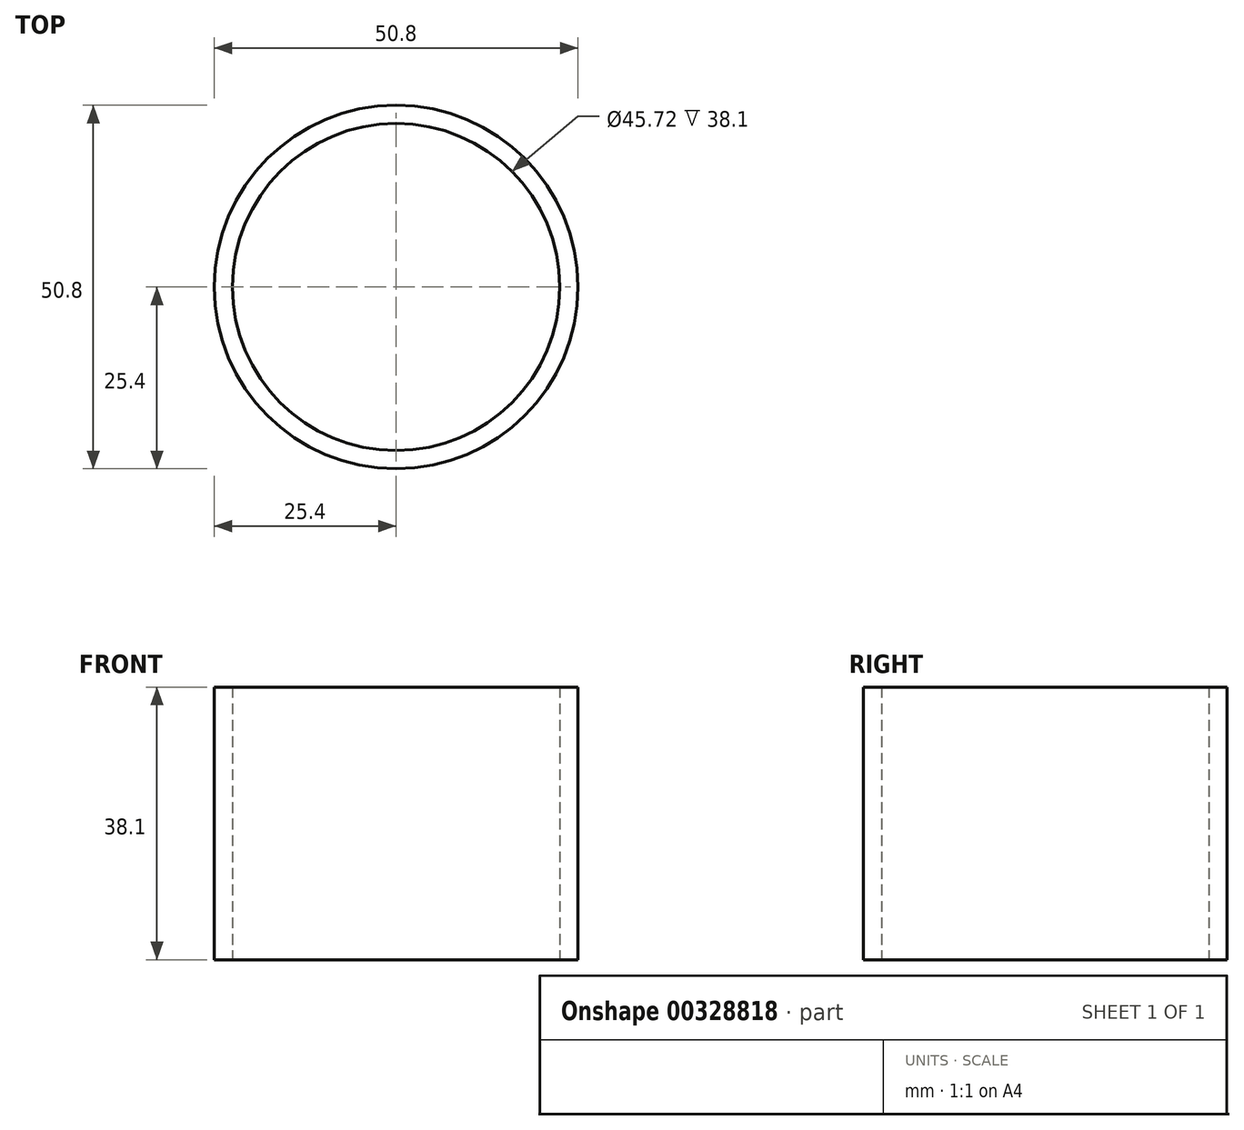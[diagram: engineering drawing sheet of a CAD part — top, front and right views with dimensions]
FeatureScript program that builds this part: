
annotation { "Feature Type Name" : "Feature", "Feature Type Description" : "" }
export const myFeature = defineFeature(function(context is Context, id is Id, definition is map)
    precondition{}
    {
        {
            var Q0;
            Q0=qCreatedBy(makeId("Top.planeOp"),FACE);
            var sketch = newSketch(context, id + "F0", { "sketchPlane" : qUnion([Q0])});
            skCircle(sketch, "E0", {"center": v(0, 0) * mm, "radius": 22.86 * mm});
            skCircle(sketch, "E1", {"center": v(0, 0) * mm, "radius": 25.4 * mm});
            skSolve(sketch);
        }
        {
            var Q0;
            Q0=makeQuery(id+"F0.imprint","IMPRINT",FACE,{"disambiguationData":[TD([[makeQuery(id+"F0.imprint","IMPRINT",EDGE,{"derivedFrom":sQuery(id+"F0.wireOp",EDGE,"E0")}),-1.0]])]});
            extrude(context, id + "F1", {"entities" : qUnion([Q0]), "depth" : 38.1 * mm});
        }
    });
